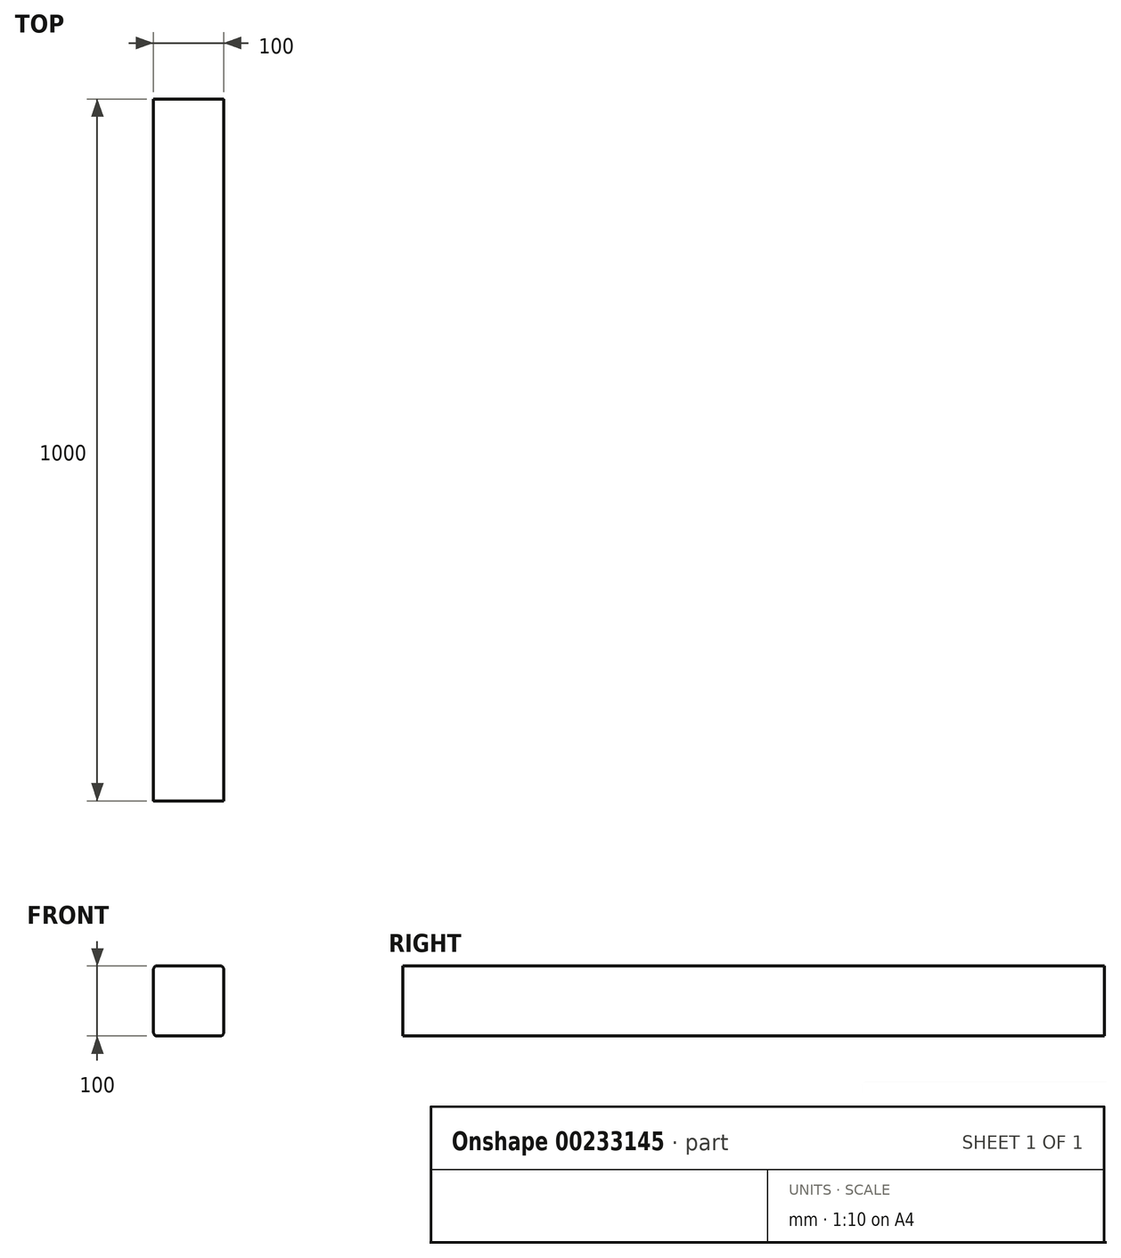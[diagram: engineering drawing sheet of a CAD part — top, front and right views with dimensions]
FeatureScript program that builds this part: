
annotation { "Feature Type Name" : "Feature", "Feature Type Description" : "" }
export const myFeature = defineFeature(function(context is Context, id is Id, definition is map)
    precondition{}
    {
        {
            var Q0;
            Q0=qCreatedBy(makeId("Front.planeOp"),FACE);
            var sketch = newSketch(context, id + "F0", { "sketchPlane" : qUnion([Q0])});
            skLineSegment(sketch, "E0.bottom", {"start": v(-761.71, 48.51) * mm, "end": v(-661.71, 48.51) * mm});
            skLineSegment(sketch, "E0.top", {"start": v(-761.71, -51.49) * mm, "end": v(-661.71, -51.49) * mm});
            skLineSegment(sketch, "E0.right", {"start": v(-661.71, -51.49) * mm, "end": v(-661.71, 48.51) * mm});
            skLineSegment(sketch, "E1.bottom", {"start": v(42.52, 48.51) * mm, "end": v(47.13, 48.51) * mm});
            skLineSegment(sketch, "E2", {"start": v(-761.71, 48.51) * mm, "end": v(-761.71, -51.49) * mm});
            skSolve(sketch);
        }
        {
            var Q0;
            Q0 = qSketchRegion(id + "F0", true);
            extrude(context, id + "F1", {"entities" : qUnion([Q0]), "endBound" : BoundingType.SYMMETRIC, "depth" : 1000 * mm});
        }
        {
            var Q0;
            Q0=makeQuery(id+"F1.opExtrude","SWEPT_EDGE",EDGE,{"disambiguationData":[OSD([sQuery(id+"F0.wireOp",EDGE,"E0.top"),sQuery(id+"F0.wireOp",EDGE,"E2")])]});
            var Q1;
            Q1=makeQuery(id+"F1.opExtrude","SWEPT_EDGE",EDGE,{"disambiguationData":[OSD([sQuery(id+"F0.wireOp",EDGE,"E0.top"),sQuery(id+"F0.wireOp",EDGE,"E0.right")])]});
            var Q2;
            Q2=makeQuery(id+"F1.opExtrude","SWEPT_EDGE",EDGE,{"disambiguationData":[OSD([sQuery(id+"F0.wireOp",EDGE,"E0.bottom"),sQuery(id+"F0.wireOp",EDGE,"E0.right")])]});
            var Q3;
            Q3=makeQuery(id+"F1.opExtrude","SWEPT_EDGE",EDGE,{"disambiguationData":[OSD([sQuery(id+"F0.wireOp",EDGE,"E0.bottom"),sQuery(id+"F0.wireOp",EDGE,"E2")])]});
            fillet(context, id + "F2", {"entities" : qUnion([Q0, Q1, Q2, Q3]), "radius" : 5 * mm, "tangentPropagation" : true, "allowEdgeOverflow" : false});
        }
    });
